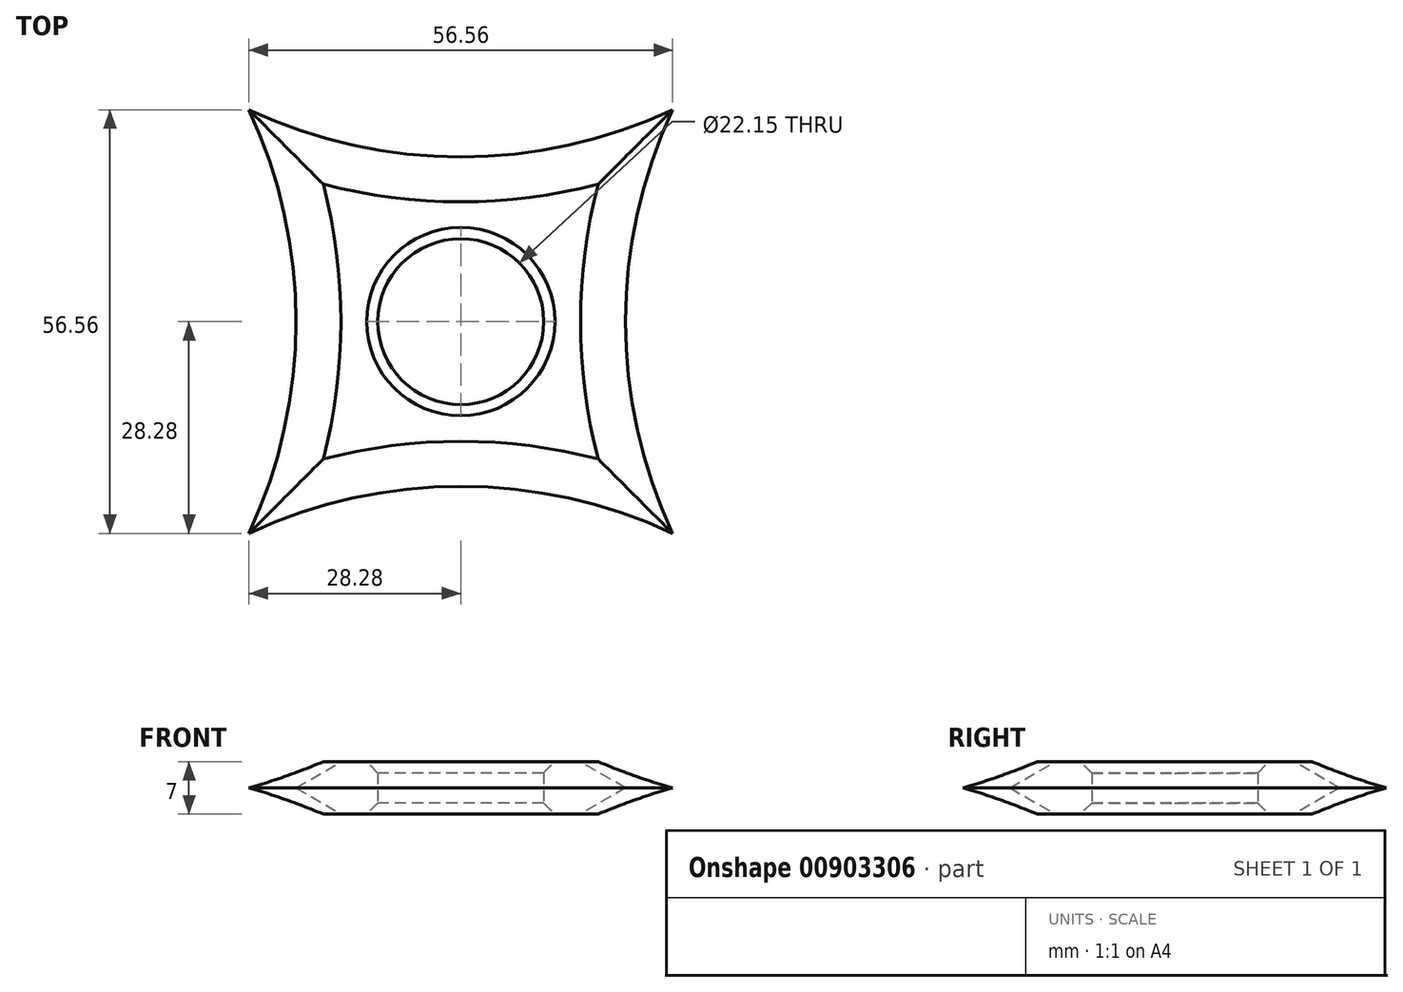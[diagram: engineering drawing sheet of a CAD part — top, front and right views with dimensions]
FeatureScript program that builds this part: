
annotation { "Feature Type Name" : "Feature", "Feature Type Description" : "" }
export const myFeature = defineFeature(function(context is Context, id is Id, definition is map)
    precondition{}
    {
        {
            var Q0;
            Q0=qCreatedBy(makeId("Top.planeOp"),FACE);
            var sketch = newSketch(context, id + "F0", { "sketchPlane" : qUnion([Q0])});
            skCircle(sketch, "E0", {"center": v(0, 0) * mm, "radius": 11.07 * mm});
            skLineSegment(sketch, "E1", {"start": v(-37.26, -37.26) * mm, "end": v(46.89, 46.89) * mm, "construction": true});
            skLineSegment(sketch, "E2", {"start": v(-28.65, 28.65) * mm, "end": v(33.8, -33.8) * mm, "construction": true});
            skArc(sketch, "E3", {"start": v(28.28, 28.28) * mm, "mid": v(22, 0) * mm, "end": v(28.28, -28.28) * mm});
            skArc(sketch, "E4.1.0", {"start": v(-28.28, 28.28) * mm, "mid": v(0, 22) * mm, "end": v(28.28, 28.28) * mm});
            skArc(sketch, "E4.2.0", {"start": v(-28.28, -28.28) * mm, "mid": v(-22, 0) * mm, "end": v(-28.28, 28.28) * mm});
            skArc(sketch, "E4.3.0", {"start": v(28.28, -28.28) * mm, "mid": v(0, -22) * mm, "end": v(-28.28, -28.28) * mm});
            skSolve(sketch);
        }
        {
            var Q0;
            Q0=makeQuery(id+"F0.imprint","IMPRINT",FACE,{"disambiguationData":[TD([[makeQuery(id+"F0.imprint","IMPRINT",EDGE,{"derivedFrom":sQuery(id+"F0.wireOp",EDGE,"E0")}),-1.0]])]});
            extrude(context, id + "F1", {"entities" : qUnion([Q0]), "depth" : 7 * mm, "offsetDistance" : 25 * mm});
        }
        {
            var Q0;
            Q0=makeQuery(id+"F1.opExtrude","CAP_EDGE",EDGE,{"disambiguationData":[OSD([sQuery(id+"F0.wireOp",EDGE,"E4.3.0")])],"isStart":false});
            var Q1;
            Q1=makeQuery(id+"F1.opExtrude","CAP_EDGE",EDGE,{"disambiguationData":[OSD([sQuery(id+"F0.wireOp",EDGE,"E4.2.0")])],"isStart":false});
            var Q2;
            Q2=makeQuery(id+"F1.opExtrude","CAP_EDGE",EDGE,{"disambiguationData":[OSD([sQuery(id+"F0.wireOp",EDGE,"E4.1.0")])],"isStart":false});
            var Q3;
            Q3=makeQuery(id+"F1.opExtrude","CAP_EDGE",EDGE,{"disambiguationData":[OSD([sQuery(id+"F0.wireOp",EDGE,"E3")])],"isStart":false});
            chamfer(context, id + "F2", {"entities" : qUnion([Q0, Q1, Q2, Q3]), "chamferType" : ChamferType.TWO_OFFSETS, "width1" : 3.5 * mm, "oppositeDirection" : false, "width2" : 6 * mm, "tangentPropagation" : true});
        }
        {
            var Q0;
            Q0=makeQuery(id+"F1.opExtrude","CAP_EDGE",EDGE,{"disambiguationData":[OSD([sQuery(id+"F0.wireOp",EDGE,"E4.2.0")])],"isStart":true});
            var Q1;
            Q1=makeQuery(id+"F1.opExtrude","CAP_EDGE",EDGE,{"disambiguationData":[OSD([sQuery(id+"F0.wireOp",EDGE,"E4.3.0")])],"isStart":true});
            var Q2;
            Q2=makeQuery(id+"F1.opExtrude","CAP_EDGE",EDGE,{"disambiguationData":[OSD([sQuery(id+"F0.wireOp",EDGE,"E3")])],"isStart":true});
            var Q3;
            Q3=makeQuery(id+"F1.opExtrude","CAP_EDGE",EDGE,{"disambiguationData":[OSD([sQuery(id+"F0.wireOp",EDGE,"E4.1.0")])],"isStart":true});
            chamfer(context, id + "F3", {"entities" : qUnion([Q0, Q1, Q2, Q3]), "chamferType" : ChamferType.TWO_OFFSETS, "width1" : 6 * mm, "oppositeDirection" : false, "width2" : 3.5 * mm, "tangentPropagation" : true});
        }
        {
            var Q0;
            Q0=makeQuery(id+"F1.opExtrude","CAP_EDGE",EDGE,{"disambiguationData":[OSD([sQuery(id+"F0.wireOp",EDGE,"E0")])],"isStart":true});
            var Q1;
            Q1=makeQuery(id+"F1.opExtrude","CAP_EDGE",EDGE,{"disambiguationData":[OSD([sQuery(id+"F0.wireOp",EDGE,"E0")])],"isStart":false});
            chamfer(context, id + "F4", {"entities" : qUnion([Q0, Q1]), "width" : 1.5 * mm, "tangentPropagation" : true});
        }
    });
